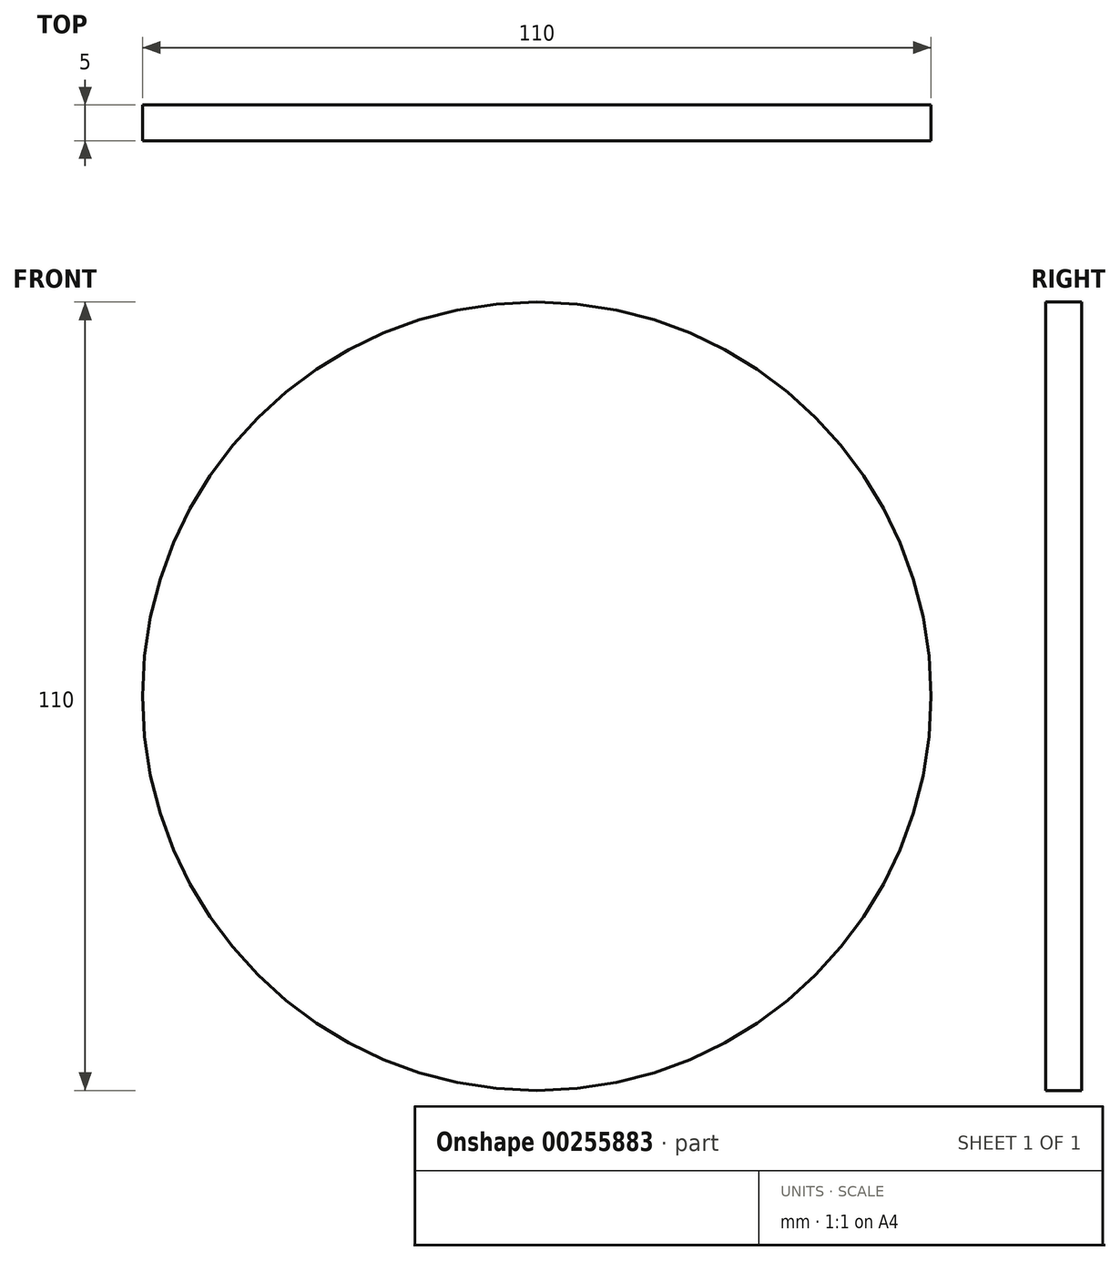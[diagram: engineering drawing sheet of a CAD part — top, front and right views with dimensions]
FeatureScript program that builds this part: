
annotation { "Feature Type Name" : "Feature", "Feature Type Description" : "" }
export const myFeature = defineFeature(function(context is Context, id is Id, definition is map)
    precondition{}
    {
        {
            var Q0;
            Q0=qCreatedBy(makeId("Front.planeOp"),FACE);
            var sketch = newSketch(context, id + "F0", { "sketchPlane" : qUnion([Q0])});
            skCircle(sketch, "E0", {"center": v(0, 0) * mm, "radius": 55 * mm});
            skSolve(sketch);
        }
        {
            var Q0;
            Q0=makeQuery(id+"F0.imprint","IMPRINT",FACE,{"disambiguationData":[TD([[makeQuery(id+"F0.imprint","IMPRINT",EDGE,{"derivedFrom":sQuery(id+"F0.wireOp",EDGE,"E0")}),1.0]])]});
            extrude(context, id + "F1", {"entities" : qUnion([Q0]), "depth" : 5 * mm});
        }
    });
